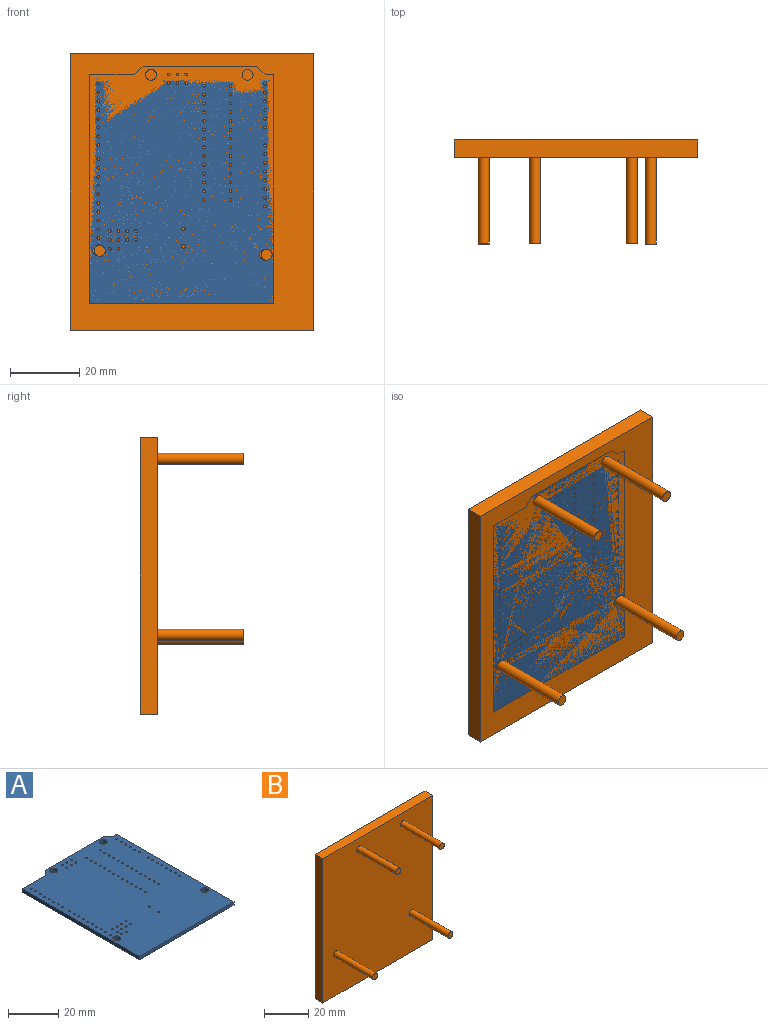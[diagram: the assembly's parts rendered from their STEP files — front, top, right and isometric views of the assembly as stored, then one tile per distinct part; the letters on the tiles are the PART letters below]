
ASSEMBLY  parts=2 mates=1
PART A: 92 faces, bbox 53.3x68.6x1.7 mm
  f0: cylinder r=0.4mm len=1.65mm, axis (0,0,1), area 4.1mm2, adj f82,f91
  f1: cylinder r=0.4mm len=1.65mm, axis (0,0,1), area 4.1mm2, adj f82,f91
  f2: cylinder r=0.4mm len=1.65mm, axis (0,0,1), area 4.1mm2, adj f82,f91
  f3: cylinder r=0.4mm len=1.65mm, axis (0,0,1), area 4.1mm2, adj f82,f91
  f4: cylinder r=0.4mm len=1.65mm, axis (0,0,1), area 4.1mm2, adj f82,f91
  f5: cylinder r=0.4mm len=1.65mm, axis (0,0,1), area 4.1mm2, adj f82,f91
  f6: cylinder r=0.4mm len=1.65mm, axis (0,0,1), area 4.1mm2, adj f82,f91
  f7: cylinder r=0.4mm len=1.65mm, axis (0,0,1), area 4.1mm2, adj f82,f91
  f8: cylinder r=0.4mm len=1.65mm, axis (0,0,1), area 4.1mm2, adj f82,f91
  f9: cylinder r=0.4mm len=1.65mm, axis (0,0,1), area 4.1mm2, adj f82,f91
  f10: cylinder r=0.4mm len=1.65mm, axis (0,0,1), area 4.1mm2, adj f82,f91
  f11: cylinder r=0.4mm len=1.65mm, axis (0,0,1), area 4.1mm2, adj f82,f91
  f12: cylinder r=0.4mm len=1.65mm, axis (0,0,1), area 4.1mm2, adj f82,f91
  f13: cylinder r=0.4mm len=1.65mm, axis (0,0,1), area 4.1mm2, adj f82,f91
  f14: cylinder r=0.4mm len=1.65mm, axis (0,0,1), area 4.1mm2, adj f82,f91
  f15: cylinder r=0.4mm len=1.65mm, axis (0,0,1), area 4.1mm2, adj f82,f91
  f16: cylinder r=0.4mm len=1.65mm, axis (0,0,1), area 4.1mm2, adj f82,f91
  f17: cylinder r=0.4mm len=1.65mm, axis (0,0,1), area 4.1mm2, adj f82,f91
  f18: cylinder r=0.4mm len=1.65mm, axis (0,0,1), area 4.1mm2, adj f82,f91
  f19: cylinder r=0.4mm len=1.65mm, axis (0,0,1), area 4.1mm2, adj f82,f91
  f20: cylinder r=0.4mm len=1.65mm, axis (0,0,1), area 4.1mm2, adj f82,f91
  f21: cylinder r=0.4mm len=1.65mm, axis (0,0,1), area 4.1mm2, adj f82,f91
  f22: cylinder r=0.4mm len=1.65mm, axis (0,0,1), area 4.1mm2, adj f82,f91
  f23: cylinder r=0.4mm len=1.65mm, axis (0,0,1), area 4.1mm2, adj f82,f91
  f24: cylinder r=0.4mm len=1.65mm, axis (0,0,1), area 4.1mm2, adj f82,f91
  f25: cylinder r=0.4mm len=1.65mm, axis (0,0,1), area 4.1mm2, adj f82,f91
  f26: cylinder r=1.59mm len=3.18mm, axis (0,0,1), area 16.5mm2, adj f82,f91
  f27: cylinder r=1.59mm len=3.18mm, axis (0,0,1), area 16.5mm2, adj f82,f91
  f28: cylinder r=1.59mm len=3.18mm, axis (0,0,1), area 16.5mm2, adj f82,f91
  f29: cylinder r=1.59mm len=3.18mm, axis (0,0,1), area 16.5mm2, adj f82,f91
  f30: cylinder r=0.4mm len=1.65mm, axis (0,0,1), area 4.1mm2, adj f82,f91
  f31: cylinder r=0.4mm len=1.65mm, axis (0,0,1), area 4.1mm2, adj f82,f91
  f32: cylinder r=0.4mm len=1.65mm, axis (0,0,1), area 4.1mm2, adj f82,f91
  f33: cylinder r=0.4mm len=1.65mm, axis (0,0,1), area 4.1mm2, adj f82,f91
  f34: cylinder r=0.4mm len=1.65mm, axis (0,0,1), area 4.1mm2, adj f82,f91
  f35: cylinder r=0.4mm len=1.65mm, axis (0,0,1), area 4.1mm2, adj f82,f91
  f36: cylinder r=0.4mm len=1.65mm, axis (0,0,1), area 4.1mm2, adj f82,f91
  f37: cylinder r=0.4mm len=1.65mm, axis (0,0,1), area 4.1mm2, adj f82,f91
  f38: cylinder r=0.4mm len=1.65mm, axis (0,0,1), area 4.1mm2, adj f82,f91
  f39: cylinder r=0.4mm len=1.65mm, axis (0,0,1), area 4.1mm2, adj f82,f91
  f40: cylinder r=0.4mm len=1.65mm, axis (0,0,1), area 4.1mm2, adj f82,f91
  f41: cylinder r=0.4mm len=1.65mm, axis (0,0,1), area 4.1mm2, adj f82,f91
  f42: cylinder r=0.4mm len=1.65mm, axis (0,0,1), area 4.1mm2, adj f82,f91
  f43: cylinder r=0.4mm len=1.65mm, axis (0,0,1), area 4.1mm2, adj f82,f91
  f44: cylinder r=0.4mm len=1.65mm, axis (0,0,1), area 4.1mm2, adj f82,f91
  f45: cylinder r=0.4mm len=1.65mm, axis (0,0,1), area 4.1mm2, adj f82,f91
  f46: cylinder r=0.4mm len=1.65mm, axis (0,0,1), area 4.1mm2, adj f82,f91
  f47: cylinder r=0.4mm len=1.65mm, axis (0,0,1), area 4.1mm2, adj f82,f91
  f48: cylinder r=0.4mm len=1.65mm, axis (0,0,1), area 4.1mm2, adj f82,f91
  f49: cylinder r=0.4mm len=1.65mm, axis (0,0,1), area 4.1mm2, adj f82,f91
  f50: cylinder r=0.4mm len=1.65mm, axis (0,0,1), area 4.1mm2, adj f82,f91
  f51: cylinder r=0.4mm len=1.65mm, axis (0,0,1), area 4.1mm2, adj f82,f91
  f52: cylinder r=0.5mm len=1.65mm, axis (0,0,1), area 5.2mm2, adj f82,f91
  f53: cylinder r=0.5mm len=1.65mm, axis (0,0,1), area 5.2mm2, adj f82,f91
  f54: cylinder r=0.4mm len=1.65mm, axis (0,0,1), area 4.1mm2, adj f82,f91
  f55: cylinder r=0.4mm len=1.65mm, axis (0,0,1), area 4.1mm2, adj f82,f91
  f56: cylinder r=0.4mm len=1.65mm, axis (0,0,1), area 4.1mm2, adj f82,f91
  f57: cylinder r=0.4mm len=1.65mm, axis (0,0,1), area 4.1mm2, adj f82,f91
  f58: cylinder r=0.4mm len=1.65mm, axis (0,0,1), area 4.1mm2, adj f82,f91
  f59: cylinder r=0.4mm len=1.65mm, axis (0,0,1), area 4.1mm2, adj f82,f91
  f60: cylinder r=0.4mm len=1.65mm, axis (0,0,1), area 4.1mm2, adj f82,f91
  f61: cylinder r=0.4mm len=1.65mm, axis (0,0,1), area 4.1mm2, adj f82,f91
  f62: cylinder r=0.4mm len=1.65mm, axis (0,0,1), area 4.1mm2, adj f82,f91
  f63: cylinder r=0.4mm len=1.65mm, axis (0,0,1), area 4.1mm2, adj f82,f91
  f64: cylinder r=0.4mm len=1.65mm, axis (0,0,1), area 4.1mm2, adj f82,f91
  f65: cylinder r=0.4mm len=1.65mm, axis (0,0,1), area 4.1mm2, adj f82,f91
  f66: cylinder r=0.4mm len=1.65mm, axis (0,0,1), area 4.1mm2, adj f82,f91
  f67: cylinder r=0.4mm len=1.65mm, axis (0,0,1), area 4.1mm2, adj f82,f91
  f68: cylinder r=0.4mm len=1.65mm, axis (0,0,1), area 4.1mm2, adj f82,f91
  f69: cylinder r=0.4mm len=1.65mm, axis (0,0,1), area 4.1mm2, adj f82,f91
  f70: cylinder r=0.4mm len=1.65mm, axis (0,0,1), area 4.1mm2, adj f82,f91
  f71: cylinder r=0.4mm len=1.65mm, axis (0,0,1), area 4.1mm2, adj f82,f91
  f72: cylinder r=0.4mm len=1.65mm, axis (0,0,1), area 4.1mm2, adj f82,f91
  f73: cylinder r=0.4mm len=1.65mm, axis (0,0,1), area 4.1mm2, adj f82,f91
  f74: cylinder r=0.4mm len=1.65mm, axis (0,0,1), area 4.1mm2, adj f82,f91
  f75: cylinder r=0.4mm len=1.65mm, axis (0,0,1), area 4.1mm2, adj f82,f91
  f76: cylinder r=0.4mm len=1.65mm, axis (0,0,1), area 4.1mm2, adj f82,f91
  f77: cylinder r=0.4mm len=1.65mm, axis (0,0,1), area 4.1mm2, adj f82,f91
  f78: cylinder r=0.4mm len=1.65mm, axis (0,0,1), area 4.1mm2, adj f82,f91
  f79: cylinder r=0.4mm len=1.65mm, axis (0,0,1), area 4.1mm2, adj f82,f91
  f80: cylinder r=0.4mm len=1.65mm, axis (0,0,1), area 4.1mm2, adj f82,f91
  f81: cylinder r=0.4mm len=1.65mm, axis (0,0,1), area 4.1mm2, adj f82,f91
  f82: plane 68.58x53.34mm, normal (0,0,1), area 3540.8mm2, adj f0,f1,f2,f3,f4,f5,f6,f7
  f83: plane 66.04x1.65mm, normal (1,0,0), area 109mm2, adj f82,f84,f90,f91
  f84: plane 2.54x1.65mm, normal (0,1,0), area 4.2mm2, adj f82,f83,f85,f91
  f85: plane 2.54x2.54mm, normal (0.71,0.71,0), area 5.9mm2, adj f82,f84,f86,f91
  f86: plane 32.77x1.65mm, normal (0,1,0), area 54.1mm2, adj f82,f85,f87,f91
  f87: plane 2.54x2.54mm, normal (-0.71,0.71,0), area 5.9mm2, adj f82,f86,f88,f91
  f88: plane 12.95x1.65mm, normal (0,1,0), area 21.4mm2, adj f82,f87,f89,f91
  f89: plane 66.04x1.65mm, normal (-1,0,0), area 109mm2, adj f82,f88,f90,f91
  f90: plane 53.34x1.65mm, normal (0,-1,0), area 88mm2, adj f82,f83,f89,f91
  f91: plane 68.58x53.34mm, normal (0,0,-1), area 3540.8mm2, adj f0,f1,f2,f3,f4,f5,f6,f7
PART B: 14 faces, bbox 70.4x30x80 mm
  f0: plane 79.95x5mm, normal (-1,0,0), area 399.8mm2, adj f1,f3,f4,f5
  f1: plane 70.39x5mm, normal (0,0,-1), area 352mm2, adj f0,f2,f4,f5
  f2: plane 79.95x5mm, normal (1,0,0), area 399.8mm2, adj f1,f3,f4,f5
  f3: plane 70.39x5mm, normal (0,0,1), area 352mm2, adj f0,f2,f4,f5
  f4: plane 79.95x70.39mm, normal (0,1,0), area 5627.9mm2, adj f0,f1,f2,f3
  f5: plane 79.95x70.39mm, normal (0,-1,0), area 5596.2mm2, adj f0,f1,f2,f3,f6,f8,f10,f12
  f6: cylinder r=1.59mm len=25mm, axis (0,1,0), area 249.4mm2, adj f5,f7
  f7: plane 3.18x3.18mm, normal (0,-1,0), area 7.9mm2, adj f6
  f8: cylinder r=1.59mm len=25mm, axis (0,1,0), area 249.4mm2, adj f5,f9
  f9: plane 3.18x3.18mm, normal (0,-1,0), area 7.9mm2, adj f8
  f10: cylinder r=1.59mm len=25mm, axis (0,1,0), area 249.4mm2, adj f5,f11
  f11: plane 3.18x3.18mm, normal (0,-1,0), area 7.9mm2, adj f10
  f12: cylinder r=1.59mm len=25mm, axis (0,1,0), area 249.4mm2, adj f5,f13
  f13: plane 3.18x3.18mm, normal (0,-1,0), area 7.9mm2, adj f12
PLACE A rot(axis=(1,0,0),90deg) t=(-5.99,-47.66,6.5)mm
PLACE B rot(axis=(0,1,0),0deg) t=(-64.88,-47.66,-1.33)mm
MATE slider A.f27 <-> B.f6  axis (0,-1,0) through (-41.55,-47.66,72.54)mm
